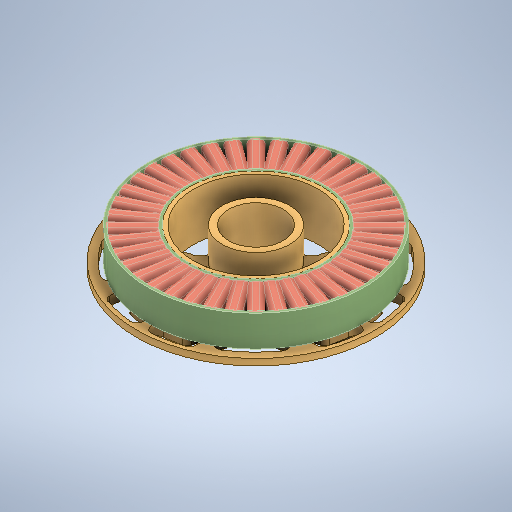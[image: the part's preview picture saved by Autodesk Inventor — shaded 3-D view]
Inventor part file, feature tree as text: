
AUTODESK INVENTOR PART (.ipt)
format: ipt  version: 2025.2 (Build 292293000, 293)  size: 1,265,664 bytes
history: native  units: in
note: dims shown in document units (in); Inventor stores cm internally (conversion verified against a paired STEP export)
features: extrude x1, sketch x1, projected_geometry x1
ambient origin geometry x8: Origin, YZ Plane, XZ Plane, XY Plane, X Axis, Y Axis, Z Axis, Center Point
bodies: Solid1 (feature_tree), Solid2 (feature_tree), Solid3 (feature_tree), Solid4 (feature_tree), Solid5 (feature_tree), Body1 (feature_tree), Body2 (feature_tree), Body3 (feature_tree), Body4 (feature_tree), Body5 (feature_tree)
feature tree (3):
  extrude  "Extrusion1"  [1 undecoded]
  sketch  "Sketch1"  dims[d0=0.25in d1=0.0in]
  projected_geometry  "Projected Loop1"
note: 1 required parameter value undecoded (feature->parameter linkage not recoverable at this tier; creation-order binding heuristic only, values carry confidence <= 0.55)
